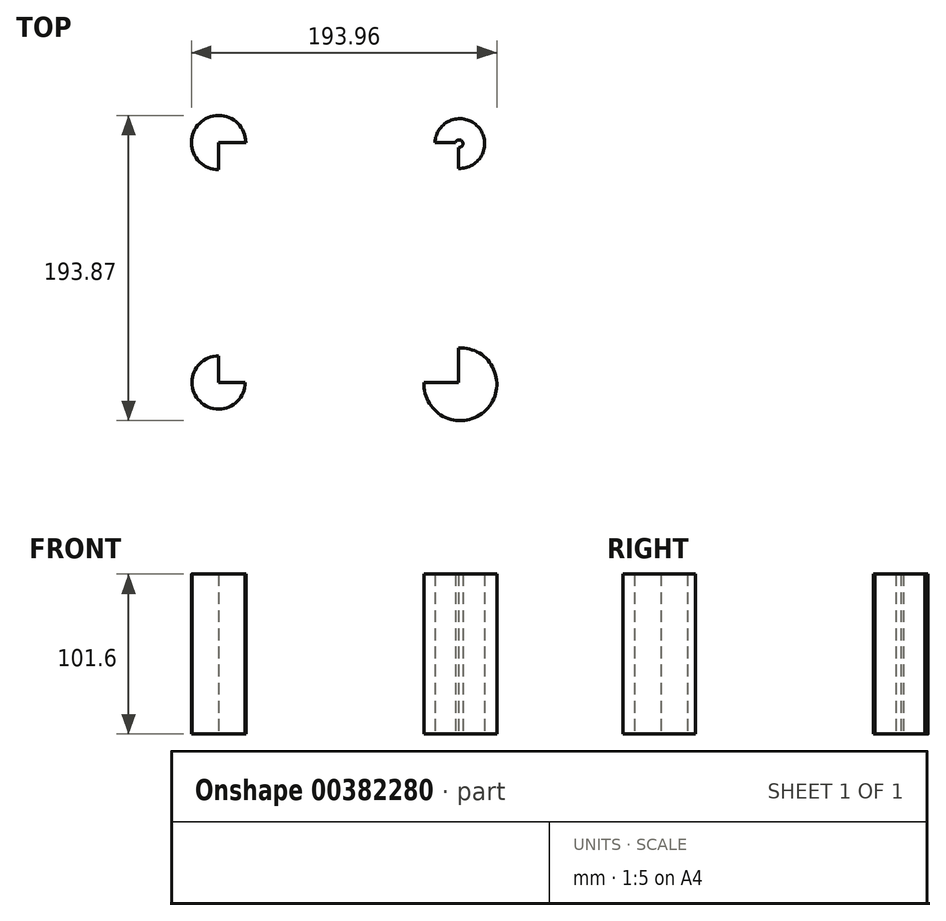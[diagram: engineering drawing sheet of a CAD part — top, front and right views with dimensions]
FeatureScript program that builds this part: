
annotation { "Feature Type Name" : "Feature", "Feature Type Description" : "" }
export const myFeature = defineFeature(function(context is Context, id is Id, definition is map)
    precondition{}
    {
        {
            var Q0;
            Q0=qCreatedBy(makeId("Top.planeOp"),FACE);
            var sketch = newSketch(context, id + "F0", { "sketchPlane" : qUnion([Q0])});
            skLineSegment(sketch, "E0.bottom", {"start": v(-76.23, 76.5) * mm, "end": v(76.23, 76.5) * mm});
            skLineSegment(sketch, "E0.top", {"start": v(-76.23, -75.83) * mm, "end": v(76.23, -75.83) * mm});
            skLineSegment(sketch, "E0.left", {"start": v(-76.23, 76.5) * mm, "end": v(-76.23, -75.83) * mm});
            skLineSegment(sketch, "E0.right", {"start": v(76.23, 76.5) * mm, "end": v(76.23, -75.83) * mm});
            skCircle(sketch, "E1", {"center": v(-76.23, 76.5) * mm, "radius": 17.28 * mm});
            skCircle(sketch, "E2", {"center": v(-76.23, -75.83) * mm, "radius": 16.85 * mm});
            skCircle(sketch, "E3", {"center": v(77.32, -76.97) * mm, "radius": 23.13 * mm});
            skCircle(sketch, "E4", {"center": v(76.49, 75.84) * mm, "radius": 2.43 * mm});
            skCircle(sketch, "E5", {"center": v(76.92, 75.87) * mm, "radius": 15.8 * mm});
            skSolve(sketch);
        }
        {
            var Q0;
            {var subQ0=sQuery(id+"F0.wireOp",EDGE,"E0.left");var subQ1=sQuery(id+"F0.wireOp",EDGE,"E0.bottom");var subQ2=makeQuery(id+"F0.imprint","INTERSECT",VERTEX,{"derivedFrom":[subQ1,subQ0]});Q0=makeQuery(id+"F0.imprint","IMPRINT",FACE,{"disambiguationData":[TD([[makeQuery(id+"F0.imprint","IMPRINT",EDGE,{"disambiguationData":[TD([[subQ2,-1.0]])],"derivedFrom":subQ1}),1.0]])]});}
            var Q1;
            {var subQ0=sQuery(id+"F0.wireOp",EDGE,"E5");var subQ1=sQuery(id+"F0.wireOp",EDGE,"E0.bottom");var subQ2=makeQuery(id+"F0.imprint","INTERSECT",VERTEX,{"derivedFrom":[subQ1,subQ0]});Q1=makeQuery(id+"F0.imprint","IMPRINT",FACE,{"disambiguationData":[TD([[makeQuery(id+"F0.imprint","IMPRINT",EDGE,{"disambiguationData":[TD([[subQ2,-1.0]])],"derivedFrom":subQ1}),1.0]])]});}
            var Q2;
            {var subQ0=sQuery(id+"F0.wireOp",EDGE,"E0.left");var subQ1=sQuery(id+"F0.wireOp",EDGE,"E0.top");var subQ2=makeQuery(id+"F0.imprint","INTERSECT",VERTEX,{"derivedFrom":[subQ1,subQ0]});Q2=makeQuery(id+"F0.imprint","IMPRINT",FACE,{"disambiguationData":[TD([[makeQuery(id+"F0.imprint","IMPRINT",EDGE,{"disambiguationData":[TD([[subQ2,-1.0]])],"derivedFrom":subQ1}),-1.0]])]});}
            var Q3;
            {var subQ0=sQuery(id+"F0.wireOp",EDGE,"E0.right");var subQ1=sQuery(id+"F0.wireOp",EDGE,"E0.top");var subQ2=makeQuery(id+"F0.imprint","INTERSECT",VERTEX,{"derivedFrom":[subQ1,subQ0]});Q3=makeQuery(id+"F0.imprint","IMPRINT",FACE,{"disambiguationData":[TD([[makeQuery(id+"F0.imprint","IMPRINT",EDGE,{"disambiguationData":[TD([[subQ2,1.0]])],"derivedFrom":subQ1}),-1.0]])]});}
            extrude(context, id + "F1", {"entities" : qUnion([Q0, Q1, Q2, Q3]), "depth" : 101.6 * mm});
        }
    });
